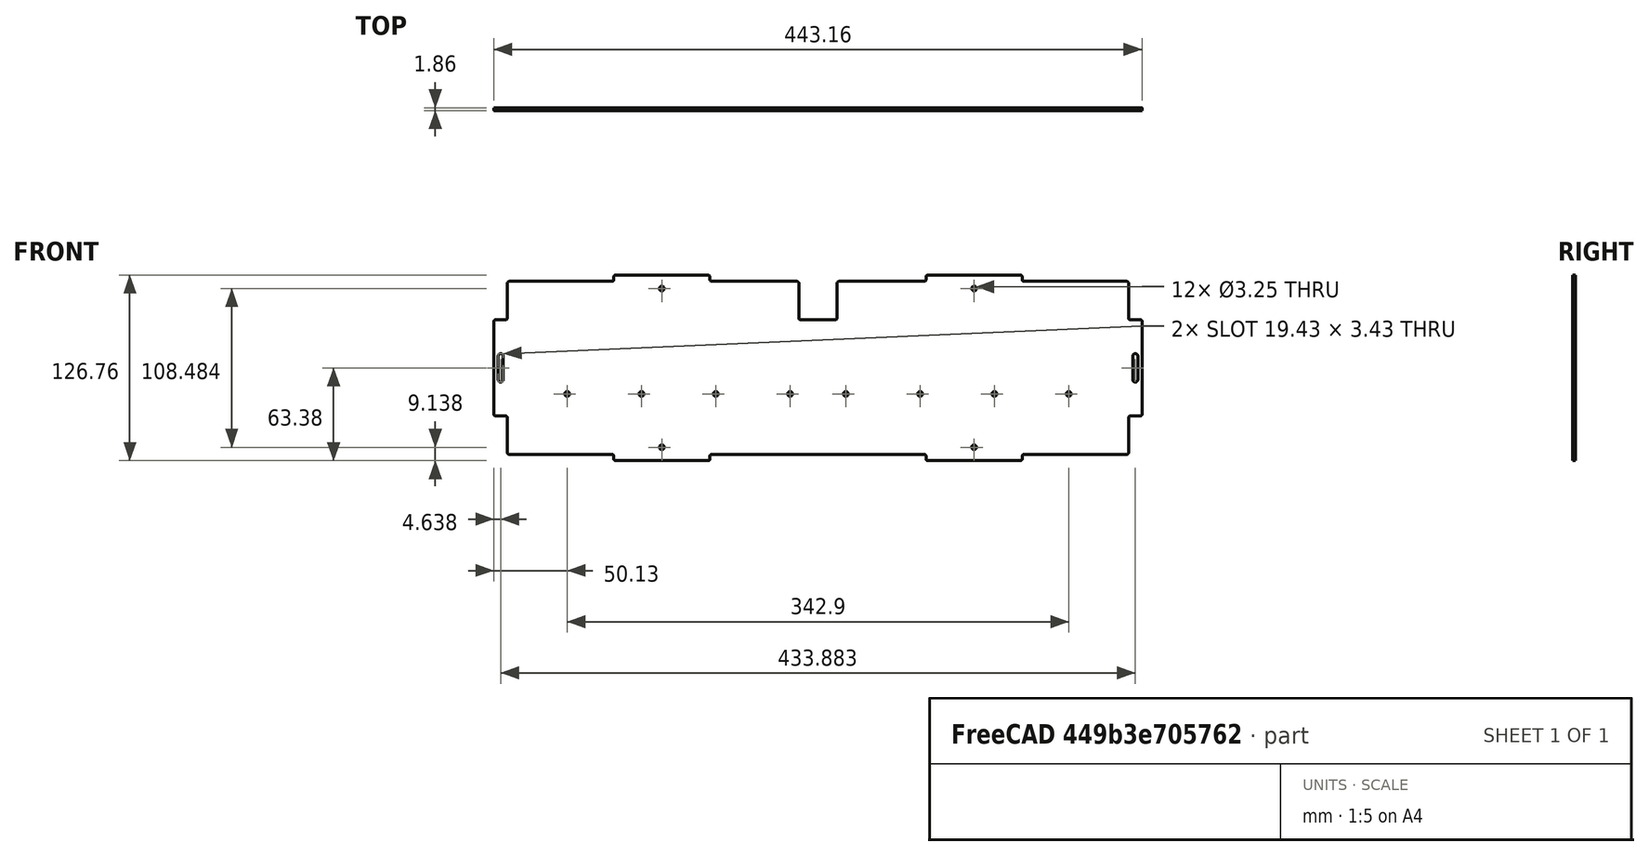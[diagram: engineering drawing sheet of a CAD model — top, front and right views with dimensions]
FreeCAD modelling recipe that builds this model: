
FCSTD DOCUMENT  (FreeCAD 1.0R38641 +468 (Git))
Label: panel_back
License: All rights reserved
LicenseURL: https://en.wikipedia.org/wiki/All_rights_reserved
objects: PartDesign::SubShapeBinder×4, Sketcher::SketchObject×1, PartDesign::Pad×1, PartDesign::Body×1
note: 10 computed .brp shape members not serialized (recipe doc carries the construction recipe); baked Part::Feature solids carry a one-line shape summary decoded from their .brp
EXTERNAL_REF file=dimensions.FCStd obj=VarSet
EXTERNAL_REF file=../third_party/doepfer_bus_board_v6.FCStd obj=Sketch
EXTERNAL_REF file=panel_top_and_bottom.FCStd obj=Body
EXTERNAL_REF file=panel_side.FCStd obj=Body001
EXTERNAL_REF file=../third_party/doepfer_bus_board_v6.FCStd obj=Body
EXTERNAL_REF file=../third_party/doepfer_psu3.FCStd obj=Body

FEATURE [PartDesign::SubShapeBinder] Binder  label="BottomPanelBinder"
  BindCopyOnChange = 0
  BindMode = 0
  ClaimChildren = false
  Context = -> Body [Binder.]
  Fuse = false
  MakeFace = true
  OffsetFill = false
  OffsetIntersection = false
  OffsetJoinType = 0
  OffsetOpenResult = false
  PartialLoad = false
  Refine = true
  Relative = true
  Support = -> [<external panel_top_and_bottom.FCStd>#Body[Pad.]]
  _Version = 2
FEATURE [PartDesign::SubShapeBinder] Binder001  label="SidePanelBinder"
  BindCopyOnChange = 0
  BindMode = 0
  ClaimChildren = false
  Context = -> Body [Binder001.]
  Fuse = false
  MakeFace = true
  OffsetFill = false
  OffsetIntersection = false
  OffsetJoinType = 0
  OffsetOpenResult = false
  PartialLoad = false
  Refine = true
  Relative = true
  Support = -> [<external panel_side.FCStd>#Body001]
  _Version = 2
FEATURE [PartDesign::SubShapeBinder] Binder002  label="BusBoardBinder"
  BindCopyOnChange = 0
  BindMode = 0
  ClaimChildren = false
  Context = -> Body [Binder002.]
  Fuse = false
  MakeFace = true
  OffsetFill = false
  OffsetIntersection = false
  OffsetJoinType = 0
  OffsetOpenResult = false
  PartialLoad = false
  Placement = pos=(0,0,0) rot=(1,0,0;1.5708rad)
  Refine = true
  Relative = true
  Support = -> [<external ../third_party/doepfer_bus_board_v6.FCStd>#Body]
  _Version = 2
FEATURE [PartDesign::SubShapeBinder] Binder003  label="PsuBinder"
  BindCopyOnChange = 0
  BindMode = 0
  ClaimChildren = false
  Context = -> Body [Binder003.]
  Fuse = false
  MakeFace = true
  OffsetFill = false
  OffsetIntersection = false
  OffsetJoinType = 0
  OffsetOpenResult = false
  PartialLoad = false
  Placement = pos=(0,0,0) rot=(1,0,0;1.5708rad)
  Refine = true
  Relative = false
  Support = -> [<external ../third_party/doepfer_psu3.FCStd>#Body]
  _Version = 2
FEATURE [Sketcher::SketchObject] Sketch
  ArcFitTolerance = 1e-06
  AttachmentOffset = pos=(0,0,0.127) rot=(0,0,1;0rad)
  AttachmentSupport = -> [Binder001,Binder]
  ExternalGeometry = -> [Binder001,Binder,Binder002,Binder003]
  FullyConstrained = true
  MakeInternals = false
  MapMode = 5
  Placement = pos=(0,127.227,2.68e-14) rot=(1,0,0;1.5708rad)
  expr: .AttachmentOffset.Base.z = dimensions#VarSet.EnclosureFinishThickness
  expr: Constraints[189] = dimensions#VarSet.EnclosureFinishThickness
  expr: Constraints[288] = doepfer_bus_board_v6#Sketch.Constraints.HoleDiameter + 2 * dimensions#VarSet.EnclosureFinishThickness
  expr: Constraints[41] = 2 * <<dimensions>>#VarSet.EnclosureFinishThickness
  expr: Constraints[47] = dimensions#VarSet.EnclosureCornerRadius
  expr: Constraints[82] = <<dimensions>>#VarSet.FrameTotalThickness - 2 * <<dimensions>>#VarSet.EnclosureFinishThickness
  expr: Constraints[83] = dimensions#VarSet.FrameMinWidth + dimensions#VarSet.FrameHoleDiameter + 2 * dimensions#VarSet.FrameFinishThickness
  expr: Constraints[84] = dimensions#VarSet.FrameTotalThickness + 2 * dimensions#VarSet.EnclosureFinishThickness
  sketch-geometry (148):
    g0: LineSegment [constr] StartX=1e-15 StartY=-23.125 StartZ=0 EndX=1e-15 EndY=-23.379 EndZ=0
    g1: LineSegment [constr] StartX=9e-16 StartY=-89.121 StartZ=0 EndX=9e-16 EndY=-89.375 EndZ=0
    g2: LineSegment StartX=1e-15 StartY=-23.379 StartZ=0 EndX=-6.8772 EndY=-23.379 EndZ=0
    g3: LineSegment StartX=-8.0772 StartY=-24.579 StartZ=0 EndX=-8.0772 EndY=-87.921 EndZ=0
    g4: LineSegment StartX=-6.8772 StartY=-89.121 StartZ=0 EndX=9e-16 EndY=-89.121 EndZ=0
    g5: LineSegment StartX=1.2 StartY=-90.321 StartZ=0 EndX=1.2 EndY=-114.173 EndZ=0
    g6: LineSegment StartX=425.8 StartY=-114.173 StartZ=0 EndX=425.8 EndY=-90.321 EndZ=0
    g7: LineSegment StartX=427 StartY=-89.121 StartZ=0 EndX=433.877 EndY=-89.121 EndZ=0
    g8: LineSegment StartX=435.077 StartY=-87.921 StartZ=0 EndX=435.077 EndY=-24.579 EndZ=0
    g9: LineSegment StartX=433.877 StartY=-23.379 StartZ=0 EndX=427 EndY=-23.379 EndZ=0
    g10: LineSegment StartX=425.8 StartY=-22.179 StartZ=0 EndX=425.8 EndY=1.6729 EndZ=0
    g11: LineSegment StartX=1.2 StartY=1.6729 StartZ=0 EndX=1.2 EndY=-22.179 EndZ=0
    g12: ArcOfCircle CenterX=424.6 CenterY=1.6729 CenterZ=0 NormalX=0 NormalY=0 NormalZ=1 AngleXU=0 Radius=1.2 StartAngle=0 EndAngle=1.5708
    g13: ArcOfCircle CenterX=427 CenterY=-22.179 CenterZ=0 NormalX=0 NormalY=0 NormalZ=1 AngleXU=0 Radius=1.2 StartAngle=3.14159 EndAngle=4.71239
    g14: ArcOfCircle CenterX=433.877 CenterY=-24.579 CenterZ=0 NormalX=0 NormalY=0 NormalZ=1 AngleXU=0 Radius=1.2 StartAngle=8e-16 EndAngle=1.5708
    g15: ArcOfCircle CenterX=433.877 CenterY=-87.921 CenterZ=0 NormalX=0 NormalY=0 NormalZ=1 AngleXU=0 Radius=1.2 StartAngle=4.71239 EndAngle=6.28319
    g16: ArcOfCircle CenterX=427 CenterY=-90.321 CenterZ=0 NormalX=0 NormalY=0 NormalZ=1 AngleXU=0 Radius=1.2 StartAngle=1.5708 EndAngle=3.14159
    g17: ArcOfCircle CenterX=424.6 CenterY=-114.173 CenterZ=0 NormalX=0 NormalY=0 NormalZ=1 AngleXU=0 Radius=1.2 StartAngle=4.71239 EndAngle=6.28319
    g18: ArcOfCircle CenterX=2.4 CenterY=-114.173 CenterZ=0 NormalX=0 NormalY=0 NormalZ=1 AngleXU=0 Radius=1.2 StartAngle=3.14159 EndAngle=4.71239
    g19: ArcOfCircle CenterX=9e-16 CenterY=-90.321 CenterZ=0 NormalX=0 NormalY=0 NormalZ=1 AngleXU=0 Radius=1.2 StartAngle=2.6e-15 EndAngle=1.5708
    g20: ArcOfCircle CenterX=-6.8772 CenterY=-87.921 CenterZ=0 NormalX=0 NormalY=0 NormalZ=1 AngleXU=0 Radius=1.2 StartAngle=3.14159 EndAngle=4.71239
    g21: ArcOfCircle CenterX=-6.8772 CenterY=-24.579 CenterZ=0 NormalX=0 NormalY=0 NormalZ=1 AngleXU=0 Radius=1.2 StartAngle=1.5708 EndAngle=3.14159
    g22: ArcOfCircle CenterX=1.2e-15 CenterY=-22.179 CenterZ=0 NormalX=0 NormalY=0 NormalZ=1 AngleXU=0 Radius=1.2 StartAngle=4.71239 EndAngle=6.28319
    g23: ArcOfCircle CenterX=2.4 CenterY=1.6729 CenterZ=0 NormalX=0 NormalY=0 NormalZ=1 AngleXU=0 Radius=1.2 StartAngle=1.5708 EndAngle=3.14159
    g24: ArcOfCircle CenterX=-3.4417 CenterY=-48.25 CenterZ=0 NormalX=0 NormalY=0 NormalZ=1 AngleXU=0 Radius=1.7145 StartAngle=8e-16 EndAngle=3.14159
    g25: ArcOfCircle CenterX=-3.4417 CenterY=-64.25 CenterZ=0 NormalX=0 NormalY=0 NormalZ=1 AngleXU=0 Radius=1.7145 StartAngle=3.14159 EndAngle=6.28319
    g26: LineSegment StartX=-1.7272 StartY=-48.25 StartZ=0 EndX=-1.7272 EndY=-64.25 EndZ=0
    g27: LineSegment StartX=-5.1562 StartY=-48.25 StartZ=0 EndX=-5.1562 EndY=-64.25 EndZ=0
    g28: LineSegment [constr] StartX=-3.4417 StartY=-48.25 StartZ=0 EndX=-3.4417 EndY=-23.379 EndZ=0
    g29: LineSegment [constr] StartX=-3.4417 StartY=-64.25 StartZ=0 EndX=-3.4417 EndY=-89.121 EndZ=0
    g30: LineSegment [constr] StartX=430.442 StartY=-23.379 StartZ=0 EndX=430.442 EndY=-48.25 EndZ=0
    g31: LineSegment [constr] StartX=430.442 StartY=-89.121 StartZ=0 EndX=430.442 EndY=-64.25 EndZ=0
    g32: ArcOfCircle CenterX=430.442 CenterY=-48.25 CenterZ=0 NormalX=0 NormalY=0 NormalZ=1 AngleXU=0 Radius=1.7145 StartAngle=-1.8e-15 EndAngle=3.14159
    g33: ArcOfCircle CenterX=430.442 CenterY=-64.25 CenterZ=0 NormalX=0 NormalY=0 NormalZ=1 AngleXU=0 Radius=1.7145 StartAngle=3.14159 EndAngle=6.28319
    g34: LineSegment StartX=432.156 StartY=-48.25 StartZ=0 EndX=432.156 EndY=-64.25 EndZ=0
    g35: LineSegment StartX=428.727 StartY=-48.25 StartZ=0 EndX=428.727 EndY=-64.25 EndZ=0
    g36: LineSegment [constr] StartX=-8.0772 StartY=-48.25 StartZ=0 EndX=-5.1562 EndY=-48.25 EndZ=0
    g37: LineSegment [constr] StartX=432.156 StartY=-48.25 StartZ=0 EndX=435.077 EndY=-48.25 EndZ=0
    g38: LineSegment StartX=72.679 StartY=2.8729 StartZ=0 EndX=2.4 EndY=2.8729 EndZ=0
    g39: LineSegment StartX=139.621 StartY=4.0729 StartZ=0 EndX=139.621 EndY=5.9271 EndZ=0
    g40: LineSegment StartX=138.421 StartY=7.1271 StartZ=0 EndX=75.079 EndY=7.1271 EndZ=0
    g41: LineSegment StartX=73.879 StartY=5.9271 StartZ=0 EndX=73.879 EndY=4.0729 EndZ=0
    g42: ArcOfCircle CenterX=72.679 CenterY=4.0729 CenterZ=0 NormalX=0 NormalY=0 NormalZ=1 AngleXU=0 Radius=1.2 StartAngle=4.71239 EndAngle=6.28319
    g43: ArcOfCircle CenterX=75.079 CenterY=5.9271 CenterZ=0 NormalX=0 NormalY=0 NormalZ=1 AngleXU=0 Radius=1.2 StartAngle=1.5708 EndAngle=3.14159
    g44: ArcOfCircle CenterX=138.421 CenterY=5.9271 CenterZ=0 NormalX=0 NormalY=0 NormalZ=1 AngleXU=0 Radius=1.2 StartAngle=1e-16 EndAngle=1.5708
    g45: ArcOfCircle CenterX=140.821 CenterY=4.0729 CenterZ=0 NormalX=0 NormalY=0 NormalZ=1 AngleXU=0 Radius=1.2 StartAngle=3.14159 EndAngle=4.71239
    g46: LineSegment StartX=353.121 StartY=4.0729 StartZ=0 EndX=353.121 EndY=5.9271 EndZ=0
    g47: LineSegment StartX=351.921 StartY=7.1271 StartZ=0 EndX=288.579 EndY=7.1271 EndZ=0
    g48: LineSegment StartX=287.379 StartY=5.9271 StartZ=0 EndX=287.379 EndY=4.0729 EndZ=0
    g49: ArcOfCircle CenterX=286.179 CenterY=4.0729 CenterZ=0 NormalX=0 NormalY=0 NormalZ=1 AngleXU=0 Radius=1.2 StartAngle=4.71239 EndAngle=6.28319
    g50: ArcOfCircle CenterX=288.579 CenterY=5.9271 CenterZ=0 NormalX=0 NormalY=0 NormalZ=1 AngleXU=0 Radius=1.2 StartAngle=1.5708 EndAngle=3.14159
    g51: ArcOfCircle CenterX=351.921 CenterY=5.9271 CenterZ=0 NormalX=0 NormalY=0 NormalZ=1 AngleXU=0 Radius=1.2 StartAngle=3e-16 EndAngle=1.5708
    g52: ArcOfCircle CenterX=354.321 CenterY=4.0729 CenterZ=0 NormalX=0 NormalY=0 NormalZ=1 AngleXU=0 Radius=1.2 StartAngle=3.14159 EndAngle=4.71239
    g53: LineSegment StartX=424.6 StartY=2.8729 StartZ=0 EndX=354.321 EndY=2.8729 EndZ=0
    g54: LineSegment StartX=2.4 StartY=-115.373 StartZ=0 EndX=72.679 EndY=-115.373 EndZ=0
    g55: LineSegment StartX=73.879 StartY=-116.573 StartZ=0 EndX=73.879 EndY=-118.427 EndZ=0
    g56: LineSegment StartX=75.079 StartY=-119.627 StartZ=0 EndX=138.421 EndY=-119.627 EndZ=0
    g57: LineSegment StartX=139.621 StartY=-118.427 StartZ=0 EndX=139.621 EndY=-116.573 EndZ=0
    g58: LineSegment StartX=140.821 StartY=-115.373 StartZ=0 EndX=286.179 EndY=-115.373 EndZ=0
    g59: LineSegment StartX=287.379 StartY=-116.573 StartZ=0 EndX=287.379 EndY=-118.427 EndZ=0
    g60: LineSegment StartX=288.579 StartY=-119.627 StartZ=0 EndX=351.921 EndY=-119.627 EndZ=0
    g61: ArcOfCircle CenterX=351.921 CenterY=-118.427 CenterZ=0 NormalX=0 NormalY=0 NormalZ=1 AngleXU=0 Radius=1.2 StartAngle=4.71239 EndAngle=6.28319
    g62: ArcOfCircle CenterX=288.579 CenterY=-118.427 CenterZ=0 NormalX=0 NormalY=0 NormalZ=1 AngleXU=0 Radius=1.2 StartAngle=3.14159 EndAngle=4.71239
    g63: ArcOfCircle CenterX=286.179 CenterY=-116.573 CenterZ=0 NormalX=0 NormalY=0 NormalZ=1 AngleXU=0 Radius=1.2 StartAngle=2.3e-15 EndAngle=1.5708
    g64: ArcOfCircle CenterX=140.821 CenterY=-116.573 CenterZ=0 NormalX=0 NormalY=0 NormalZ=1 AngleXU=0 Radius=1.2 StartAngle=1.5708 EndAngle=3.14159
    g65: ArcOfCircle CenterX=138.421 CenterY=-118.427 CenterZ=0 NormalX=0 NormalY=0 NormalZ=1 AngleXU=0 Radius=1.2 StartAngle=4.71239 EndAngle=6.28319
    g66: ArcOfCircle CenterX=75.079 CenterY=-118.427 CenterZ=0 NormalX=0 NormalY=0 NormalZ=1 AngleXU=0 Radius=1.2 StartAngle=3.14159 EndAngle=4.71239
    g67: ArcOfCircle CenterX=72.679 CenterY=-116.573 CenterZ=0 NormalX=0 NormalY=0 NormalZ=1 AngleXU=0 Radius=1.2 StartAngle=5.1e-15 EndAngle=1.5708
    g68: LineSegment StartX=353.121 StartY=-118.427 StartZ=0 EndX=353.121 EndY=-116.573 EndZ=0
    g69: ArcOfCircle CenterX=354.321 CenterY=-116.573 CenterZ=0 NormalX=0 NormalY=0 NormalZ=1 AngleXU=0 Radius=1.2 StartAngle=1.5708 EndAngle=3.14159
    g70: LineSegment StartX=354.321 StartY=-115.373 StartZ=0 EndX=424.6 EndY=-115.373 EndZ=0
    g71: LineSegment [constr] StartX=73.625 StartY=4.0729 StartZ=0 EndX=73.879 EndY=4.0729 EndZ=0
    g72: LineSegment [constr] StartX=139.621 StartY=4.0729 StartZ=0 EndX=139.875 EndY=4.0729 EndZ=0
    g73: LineSegment [constr] StartX=287.125 StartY=4.0729 StartZ=0 EndX=287.379 EndY=4.0729 EndZ=0
    g74: LineSegment [constr] StartX=353.121 StartY=4.0729 StartZ=0 EndX=353.375 EndY=4.0729 EndZ=0
    g75: Circle CenterX=194.45 CenterY=-74.03 CenterZ=0 NormalX=0 NormalY=0 NormalZ=1 AngleXU=0 Radius=1.627
    g76: Circle CenterX=232.55 CenterY=-74.03 CenterZ=0 NormalX=0 NormalY=0 NormalZ=1 AngleXU=0 Radius=1.627
    g77: Circle CenterX=283.35 CenterY=-74.03 CenterZ=0 NormalX=0 NormalY=0 NormalZ=1 AngleXU=0 Radius=1.627
    g78: Circle CenterX=334.15 CenterY=-74.03 CenterZ=0 NormalX=0 NormalY=0 NormalZ=1 AngleXU=0 Radius=1.627
    g79: Circle CenterX=384.95 CenterY=-74.03 CenterZ=0 NormalX=0 NormalY=0 NormalZ=1 AngleXU=0 Radius=1.627
    g80: Circle CenterX=143.65 CenterY=-74.03 CenterZ=0 NormalX=0 NormalY=0 NormalZ=1 AngleXU=0 Radius=1.627
    g81: Circle CenterX=92.85 CenterY=-74.03 CenterZ=0 NormalX=0 NormalY=0 NormalZ=1 AngleXU=0 Radius=1.627
    g82: Circle CenterX=42.05 CenterY=-74.03 CenterZ=0 NormalX=0 NormalY=0 NormalZ=1 AngleXU=0 Radius=1.627
    g83: LineSegment [constr] StartX=42.05 StartY=-74.03 StartZ=0 EndX=92.85 EndY=-74.03 EndZ=0
    g84: LineSegment [constr] StartX=92.85 StartY=-74.03 StartZ=0 EndX=143.65 EndY=-74.03 EndZ=0
    g85: LineSegment [constr] StartX=143.65 StartY=-74.03 StartZ=0 EndX=194.45 EndY=-74.03 EndZ=0
    g86: LineSegment [constr] StartX=194.45 StartY=-74.03 StartZ=0 EndX=232.55 EndY=-74.03 EndZ=0
    g87: LineSegment [constr] StartX=232.55 StartY=-74.03 StartZ=0 EndX=283.35 EndY=-74.03 EndZ=0
    g88: LineSegment [constr] StartX=283.35 StartY=-74.03 StartZ=0 EndX=334.15 EndY=-74.03 EndZ=0
    g89: LineSegment [constr] StartX=334.15 StartY=-74.03 StartZ=0 EndX=384.95 EndY=-74.03 EndZ=0
    g90: LineSegment [constr] StartX=176.53 StartY=3.175 StartZ=0 EndX=214.63 EndY=3.175 EndZ=0
    g91: LineSegment [constr] StartX=214.63 StartY=3.175 StartZ=0 EndX=265.43 EndY=3.175 EndZ=0
    g92: LineSegment [constr] StartX=367.03 StartY=3.175 StartZ=0 EndX=391.16 EndY=3.175 EndZ=0
    g93: LineSegment [constr] StartX=384.95 StartY=-74.03 StartZ=0 EndX=409.08 EndY=-74.03 EndZ=0
    g94: LineSegment [constr] StartX=384.95 StartY=-74.03 StartZ=0 EndX=384.95 EndY=-35.295 EndZ=0
    g95: LineSegment [constr] StartX=409.08 StartY=-35.295 StartZ=0 EndX=42.05 EndY=-35.295 EndZ=0
    g96: LineSegment [constr] StartX=42.05 StartY=-74.03 StartZ=0 EndX=42.05 EndY=-35.295 EndZ=0
    g97: LineSegment [constr] StartX=409.08 StartY=-74.03 StartZ=0 EndX=409.08 EndY=-35.295 EndZ=0
    g98: LineSegment [constr] StartX=367.03 StartY=3.175 StartZ=0 EndX=367.03 EndY=41.91 EndZ=0
    g99: LineSegment [constr] StartX=367.03 StartY=3.175 StartZ=0 EndX=367.03 EndY=-5.6e-14 EndZ=0
    g100: LineSegment [constr] StartX=384.95 StartY=-74.03 StartZ=0 EndX=384.95 EndY=-77.205 EndZ=0
    g101: LineSegment [constr] StartX=409.08 StartY=-74.03 StartZ=0 EndX=409.08 EndY=-77.205 EndZ=0
    g102: LineSegment [constr] StartX=384.95 StartY=-77.205 StartZ=0 EndX=409.08 EndY=-77.205 EndZ=0
    g103: LineSegment [constr] StartX=409.08 StartY=-35.295 StartZ=0 EndX=409.08 EndY=2.8729 EndZ=0
    g104: LineSegment [constr] StartX=409.08 StartY=-77.205 StartZ=0 EndX=409.08 EndY=-115.373 EndZ=0
    g105: LineSegment [constr] StartX=42.05 StartY=-74.03 StartZ=0 EndX=17.92 EndY=-74.03 EndZ=0
    g106: LineSegment [constr] StartX=17.92 StartY=-74.03 StartZ=0 EndX=17.92 EndY=-35.295 EndZ=0
    g107: LineSegment [constr] StartX=17.92 StartY=-35.295 StartZ=0 EndX=42.05 EndY=-35.295 EndZ=0
    g108: LineSegment [constr] StartX=17.92 StartY=-35.295 StartZ=0 EndX=-8.0772 EndY=-35.295 EndZ=0
    g109: LineSegment [constr] StartX=409.08 StartY=-35.295 StartZ=0 EndX=435.077 EndY=-35.295 EndZ=0
    g110: LineSegment [constr] StartX=314 StartY=-16.25 StartZ=0 EndX=314 EndY=-96.25 EndZ=0
    g111: LineSegment [constr] StartX=113 StartY=-16.25 StartZ=0 EndX=113 EndY=-96.25 EndZ=0
    g112: LineSegment [constr] StartX=113 StartY=-16.25 StartZ=0 EndX=314 EndY=-16.25 EndZ=0
    g113: LineSegment [constr] StartX=113 StartY=-96.25 StartZ=0 EndX=314 EndY=-96.25 EndZ=0
    g114: LineSegment [constr] StartX=106.75 StartY=-2.0081 StartZ=0 EndX=320.25 EndY=-2.0081 EndZ=0
    g115: LineSegment [constr] StartX=106.75 StartY=-110.492 StartZ=0 EndX=320.25 EndY=-110.492 EndZ=0
    g116: Circle CenterX=106.75 CenterY=-2.0081 CenterZ=0 NormalX=0 NormalY=0 NormalZ=1 AngleXU=0 Radius=1.627
    g117: Circle CenterX=106.75 CenterY=-110.492 CenterZ=0 NormalX=0 NormalY=0 NormalZ=1 AngleXU=0 Radius=1.627
    g118: Circle CenterX=320.25 CenterY=-110.492 CenterZ=0 NormalX=0 NormalY=0 NormalZ=1 AngleXU=0 Radius=1.627
    g119: Circle CenterX=320.25 CenterY=-2.0081 CenterZ=0 NormalX=0 NormalY=0 NormalZ=1 AngleXU=0 Radius=1.627
    g120: LineSegment [constr] StartX=286.179 StartY=2.8729 StartZ=0 EndX=354.321 EndY=2.8729 EndZ=0
    g121: LineSegment [constr] StartX=320.25 StartY=-3.6351 StartZ=0 EndX=320.25 EndY=-110.492 EndZ=0
    g122: LineSegment [constr] StartX=320.25 StartY=-0.3811 StartZ=0 EndX=320.25 EndY=2.8729 EndZ=0
    g123: LineSegment [constr] StartX=320.25 StartY=-0.3811 StartZ=0 EndX=320.25 EndY=-3.6351 EndZ=0
    g124: LineSegment [constr] StartX=72.679 StartY=2.8729 StartZ=0 EndX=140.821 EndY=2.8729 EndZ=0
    g125: LineSegment [constr] StartX=106.75 StartY=-2.0081 StartZ=0 EndX=106.75 EndY=-110.492 EndZ=0
    g126: LineSegment [constr] StartX=72.679 StartY=-115.373 StartZ=0 EndX=140.821 EndY=-115.373 EndZ=0
    g127: LineSegment [constr] StartX=286.179 StartY=-115.373 StartZ=0 EndX=354.321 EndY=-115.373 EndZ=0
    g128: LineSegment [constr] StartX=320.25 StartY=-115.373 StartZ=0 EndX=320.25 EndY=-110.492 EndZ=0
    g129: LineSegment [constr] StartX=106.75 StartY=-2.0081 StartZ=0 EndX=106.75 EndY=2.8729 EndZ=0
    g130: LineSegment [constr] StartX=106.75 StartY=-16.25 StartZ=0 EndX=113 EndY=-16.25 EndZ=0
    g131: LineSegment [constr] StartX=314 StartY=-16.25 StartZ=0 EndX=320.25 EndY=-16.25 EndZ=0
    g132: LineSegment [constr] StartX=113 StartY=-16.25 StartZ=0 EndX=113 EndY=-2.0081 EndZ=0
    g133: LineSegment [constr] StartX=113 StartY=-96.25 StartZ=0 EndX=113 EndY=-110.492 EndZ=0
    g134: LineSegment StartX=199.174 StartY=2.8729 StartZ=0 EndX=140.821 EndY=2.8729 EndZ=0
    g135: LineSegment StartX=200.374 StartY=-22.179 StartZ=0 EndX=200.374 EndY=1.6729 EndZ=0
    g136: LineSegment StartX=225.426 StartY=-23.379 StartZ=0 EndX=201.574 EndY=-23.379 EndZ=0
    g137: LineSegment StartX=286.179 StartY=2.8729 StartZ=0 EndX=227.826 EndY=2.8729 EndZ=0
    g138: LineSegment StartX=226.626 StartY=1.6729 StartZ=0 EndX=226.626 EndY=-22.179 EndZ=0
    g139: ArcOfCircle CenterX=199.174 CenterY=1.6729 CenterZ=0 NormalX=0 NormalY=0 NormalZ=1 AngleXU=0 Radius=1.2 StartAngle=1e-16 EndAngle=1.5708
    g140: GeomPoint [constr] X=200.374 Y=2.8729 Z=0
    g141: ArcOfCircle CenterX=201.574 CenterY=-22.179 CenterZ=0 NormalX=0 NormalY=0 NormalZ=1 AngleXU=0 Radius=1.2 StartAngle=3.14159 EndAngle=4.71239
    g142: GeomPoint [constr] X=200.374 Y=-23.379 Z=0
    g143: ArcOfCircle CenterX=225.426 CenterY=-22.179 CenterZ=0 NormalX=0 NormalY=0 NormalZ=1 AngleXU=0 Radius=1.2 StartAngle=4.71239 EndAngle=6.28319
    g144: GeomPoint [constr] X=226.626 Y=-23.379 Z=0
    g145: ArcOfCircle CenterX=227.826 CenterY=1.6729 CenterZ=0 NormalX=0 NormalY=0 NormalZ=1 AngleXU=0 Radius=1.2 StartAngle=1.5708 EndAngle=3.14159
    g146: GeomPoint [constr] X=226.626 Y=2.8729 Z=0
    g147: LineSegment [constr] StartX=213.5 StartY=-115.373 StartZ=0 EndX=213.5 EndY=-23.379 EndZ=0
  constraints (388):
    c: Equal(g1,g0)
    c: Horizontal(g2)
    c: Vertical(g3)
    c: Horizontal(g4)
    c: Vertical(g5)
    c: Vertical(g6)
    c: Horizontal(g7)
    c: Vertical(g8)
    c: Horizontal(g9)
    c: Vertical(g10)
    c: Vertical(g11)
    c: Tangent(g10,g12) = -1.5708
    c: Tangent(g9,g13) = 1.5708
    c: Tangent(g10,g13) = 1.5708
    c: Tangent(g8,g14) = -1.5708
    c: Tangent(g9,g14) = -1.5708
    c: Tangent(g7,g15) = -1.5708
    c: Tangent(g8,g15) = -1.5708
    c: Tangent(g6,g16) = 1.5708
    c: Tangent(g7,g16) = 1.5708
    c: Tangent(g6,g17) = -1.5708
    c: Tangent(g5,g18) = -1.5708
    c: Tangent(g4,g19) = 1.5708
    c: Tangent(g5,g19) = 1.5708
    c: Tangent(g3,g20) = -1.5708
    c: Tangent(g4,g20) = -1.5708
    c: Tangent(g2,g21) = -1.5708
    c: Tangent(g3,g21) = -1.5708
    c: Tangent(g2,g22) = 1.5708
    c: Tangent(g11,g22) = 1.5708
    c: Tangent(g11,g23) = -1.5708
    c: Equal(g12,g13)
    c: Equal(g13,g14)
    c: Equal(g14,g15)
    c: Equal(g15,g16)
    c: Equal(g16,g17)
    c: Equal(g18,g19)
    c: Equal(g19,g20)
    c: Equal(g20,g21)
    c: Equal(g21,g22)
    c: Equal(g22,g23)
    c: Distance(g1,g1) = 0.254
    c: Equal(g5,g11)
    c: Equal(g5,g6)
    c: Equal(g8,g3)
    c: Equal(g11,g10)
    c: Equal(g4,g7)
    c: Radius(g23) = 1.2
    c: Equal(g9,g7)
    c: Tangent(g24,g26) = 1.5708
    c: Tangent(g24,g27) = -1.5708
    c: Tangent(g25,g26) = 1.5708
    c: Tangent(g25,g27) = -1.5708
    c: Equal(g24,g25)
    c: Vertical(g26)
    c: Coincident(g29,g25)
    c: Vertical(g29)
    c: Equal(g28,g29)
    c: Coincident(g28,g24)
    c: Vertical(g28)
    c: PointOnObject(g30,g9)
    c: Vertical(g30)
    c: PointOnObject(g31,g7)
    c: Vertical(g31)
    c: Tangent(g32,g34) = 1.5708
    c: Tangent(g32,g35) = -1.5708
    c: Tangent(g33,g34) = 1.5708
    c: Tangent(g33,g35) = -1.5708
    c: Equal(g32,g33)
    c: Coincident(g32,g30)
    c: Coincident(g33,g31)
    c: Vertical(g34)
    c: Equal(g30,g31)
    c: Equal(g28,g30)
    c: Equal(g32,g24)
    c: PointOnObject(g36,g3)
    c: Coincident(g36,g24)
    c: Horizontal(g36)
    c: Coincident(g37,g32)
    c: PointOnObject(g37,g8)
    c: Horizontal(g37)
    c: Equal(g37,g36)
    c: Distance(g36,g36) = 2.921
    c: DistanceY(g27,g27) = 16
    c: Diameter(g24) = 3.429
    c: Vertical(g1)
    c: Vertical(g0)
    c: Horizontal(g53)
    c: Vertical(g46)
    c: Horizontal(g47)
    c: Vertical(g48)
    c: Vertical(g39)
    c: Horizontal(g40)
    c: Vertical(g41)
    c: Tangent(g41,g42) = 1.5708
    c: Tangent(g38,g42) = 1.5708
    c: Tangent(g40,g43) = -1.5708
    c: Tangent(g41,g43) = -1.5708
    c: Tangent(g39,g44) = -1.5708
    c: Tangent(g40,g44) = -1.5708
    c: Coincident(g134,g45) = 1.5708
    c: Tangent(g39,g45) = 1.5708
    c: Tangent(g48,g49) = 1.5708
    c: Tangent(g47,g50) = -1.5708
    c: Tangent(g48,g50) = -1.5708
    c: Tangent(g46,g51) = -1.5708
    c: Tangent(g47,g51) = -1.5708
    c: Tangent(g53,g52) = 1.5708
    c: Tangent(g46,g52) = 1.5708
    c: Equal(g42,g43)
    c: Equal(g43,g44)
    c: Equal(g44,g45)
    c: Equal(g45,g49)
    c: Equal(g49,g50)
    c: Equal(g51,g52)
    c: Equal(g50,g51)
    c: Equal(g48,g39)
    c: Horizontal(g38)
    c: Horizontal(g54)
    c: Vertical(g55)
    c: Horizontal(g56)
    c: Vertical(g57)
    c: Horizontal(g58)
    c: Vertical(g59)
    c: Horizontal(g60)
    c: Vertical(g68)
    c: Horizontal(g70)
    c: Tangent(g68,g69) = 1.5708
    c: Tangent(g70,g69) = 1.5708
    c: Tangent(g60,g61) = -1.5708
    c: Tangent(g68,g61) = -1.5708
    c: Tangent(g59,g62) = -1.5708
    c: Tangent(g60,g62) = -1.5708
    c: Tangent(g58,g63) = 1.5708
    c: Tangent(g59,g63) = 1.5708
    c: Tangent(g57,g64) = 1.5708
    c: Tangent(g58,g64) = 1.5708
    c: Tangent(g56,g65) = -1.5708
    c: Tangent(g57,g65) = -1.5708
    c: Tangent(g55,g66) = -1.5708
    c: Tangent(g56,g66) = -1.5708
    c: Tangent(g54,g67) = 1.5708
    c: Tangent(g55,g67) = 1.5708
    c: Equal(g69,g61)
    c: Equal(g61,g62)
    c: Equal(g62,g63)
    c: Equal(g64,g65)
    c: Equal(g65,g66)
    c: Equal(g66,g67)
    c: Equal(g57,g59)
    c: Equal(g54,g70)
    c: Tangent(g17,g70) = -1.5708
    c: Tangent(g12,g53) = -1.5708
    c: Tangent(g54,g18) = -1.5708
    c: Tangent(g23,g38) = -1.5708
    c: Coincident(g0,g2)
    c: Coincident(g1,g4)
    c: PointOnObject(g29,g4)
    c: PointOnObject(g28,g2)
    c: Coincident(g0,g-4)
    c: Coincident(g-4,g1)
    c: Equal(g23,g42)
    c: Equal(g18,g67)
    c: Equal(g63,g64)
    c: Coincident(g71,g41)
    c: Horizontal(g71)
    c: Equal(g71,g0)
    c: Coincident(g72,g39)
    c: Equal(g71,g72)
    c: Coincident(g73,g48)
    c: Coincident(g74,g46)
    c: Horizontal(g74)
    c: Equal(g74,g73)
    c: Equal(g73,g72)
    c: Distance(g73,g73) = 0.254
    c: Distance(g74,g74) = 0.254
    c: Distance(g72,g72) = 0.254
    c: Distance(g71,g71) = 0.254
    c: Distance(g0,g0) = 0.254
    c: Equal(g54,g38)
    c: Coincident(g74,g-6)
    c: Coincident(g73,g-6)
    c: Coincident(g72,g-5)
    c: Coincident(g71,g-5)
    c: Equal(g55,g41)
    c: Equal(g57,g55)
    c: Equal(g56,g40)
    c: Equal(g60,g47)
    c: Equal(g59,g68)
    c: Distance(g26,g-3) = 0.127
    c: PointOnObject(g41,g-8)
    c: DistanceX(g47,g47) = 63.342
    c: DistanceX(g40,g40) = 63.342
    c: DistanceY(g3,g3) = 63.342
    c: Equal(g82,g81)
    c: Equal(g81,g80)
    c: Equal(g80,g75)
    c: Equal(g75,g76)
    c: Equal(g76,g77)
    c: Equal(g77,g78)
    c: Equal(g78,g79)
    c: Coincident(g83,g82)
    c: Coincident(g83,g81)
    c: Horizontal(g83)
    c: Coincident(g84,g81)
    c: Coincident(g84,g80)
    c: Coincident(g85,g80)
    c: Coincident(g85,g75)
    c: Coincident(g86,g75)
    c: Coincident(g86,g76)
    c: Horizontal(g86)
    c: Coincident(g87,g76)
    c: Coincident(g87,g77)
    c: Coincident(g88,g77)
    c: Coincident(g88,g78)
    c: Horizontal(g88)
    c: Coincident(g89,g78)
    c: Coincident(g89,g79)
    c: Horizontal(g89)
    c: Horizontal(g87)
    c: Horizontal(g85)
    c: Horizontal(g84)
    c: Equal(g83,g84)
    c: Equal(g84,g85)
    c: Equal(g85,g87)
    c: Equal(g87,g88)
    c: Equal(g88,g89)
    c: Coincident(g90,g-9)
    c: Coincident(g90,g-10)
    c: Coincident(g91,g90)
    c: Coincident(g91,g-11)
    c: Equal(g90,g86)
    c: Equal(g91,g87)
    c: Coincident(g92,g-14)
    c: PointOnObject(g92,g-13)
    c: Horizontal(g92)
    c: Coincident(g93,g79)
    c: Horizontal(g93)
    c: Coincident(g94,g79)
    c: Vertical(g94)
    c: Horizontal(g95)
    c: Coincident(g96,g82)
    c: Coincident(g96,g95)
    c: Vertical(g96)
    c: Coincident(g97,g93)
    c: Coincident(g97,g95)
    c: Vertical(g97)
    c: PointOnObject(g94,g95)
    c: Coincident(g98,g92)
    c: PointOnObject(g98,g-12)
    c: Vertical(g98)
    c: Equal(g98,g94)
    c: Equal(g93,g92)
    c: Coincident(g99,g92)
    c: PointOnObject(g99,g-15)
    c: Vertical(g99)
    c: Coincident(g100,g79)
    c: Coincident(g101,g93)
    c: Vertical(g101)
    c: Coincident(g102,g100)
    c: Coincident(g102,g101)
    c: Vertical(g100)
    c: Horizontal(g102)
    c: Equal(g100,g99)
    c: Coincident(g103,g95)
    c: PointOnObject(g103,g53)
    c: Vertical(g103)
    c: Coincident(g104,g101)
    c: PointOnObject(g104,g70)
    c: Vertical(g104)
    c: Equal(g104,g103)
    c: Coincident(g105,g82)
    c: Horizontal(g105)
    c: Coincident(g106,g105)
    c: Vertical(g106)
    c: Coincident(g107,g95)
    c: Horizontal(g107)
    c: Coincident(g107,g106)
    c: Coincident(g108,g106)
    c: PointOnObject(g108,g3)
    c: Horizontal(g108)
    c: Coincident(g109,g95)
    c: PointOnObject(g109,g8)
    c: Horizontal(g109)
    c: Equal(g109,g108)
    c: Equal(g105,g93)
    c: DistanceX(g85,g85) = 50.8
    c: DistanceX(g86,g86) = 38.1
    c: Diameter(g80) = 3.254
    c: Vertical(g110)
    c: Vertical(g111)
    c: Coincident(g112,g111)
    c: Coincident(g112,g110)
    c: Coincident(g113,g111)
    c: Coincident(g113,g110)
    c: Horizontal(g113)
    c: Equal(g112,g-17)
    c: Equal(g110,g-16)
    c: Horizontal(g114)
    c: Horizontal(g115)
    c: Coincident(g117,g115)
    c: Coincident(g118,g115)
    c: Equal(g119,g118)
    c: Equal(g118,g117)
    c: Equal(g116,g117)
    c: Equal(g116,g80)
    c: Coincident(g120,g137)
    c: Coincident(g120,g52)
    c: Coincident(g121,g115)
    c: Vertical(g121)
    c: PointOnObject(g122,g119)
    c: PointOnObject(g122,g120)
    c: PointOnObject(g121,g119)
    c: Tangent(g121,g122)
    c: Coincident(g123,g122)
    c: Coincident(g123,g121)
    c: PointOnObject(g119,g123)
    c: Equal(g123,g122)
    c: Coincident(g114,g119)
    c: Equal(g114,g115)
    c: Coincident(g124,g38)
    c: Tangent(g124,g45) = -1.5708
    c: Coincident(g125,g115)
    c: Coincident(g126,g54)
    c: Coincident(g126,g58)
    c: Vertical(g128)
    c: Coincident(g128,g115)
    c: Symmetric(g127,g127,g128)
    c: Coincident(g127,g58)
    c: Coincident(g127,g69)
    c: Coincident(g125,g116)
    c: Coincident(g114,g116)
    c: Coincident(g129,g114)
    c: Symmetric(g124,g124,g129)
    c: Vertical(g129)
    c: Equal(g129,g128)
    c: PointOnObject(g130,g125)
    c: Coincident(g130,g111)
    c: Horizontal(g130)
    c: Coincident(g131,g110)
    c: PointOnObject(g131,g121)
    c: Horizontal(g131)
    c: Equal(g131,g130)
    c: Coincident(g132,g111)
    c: PointOnObject(g132,g114)
    c: Vertical(g132)
    c: Coincident(g133,g111)
    c: PointOnObject(g133,g115)
    c: Vertical(g133)
    c: Equal(g133,g132)
    c: Horizontal(g112)
    c: Horizontal(g134)
    c: Horizontal(g137)
    c: Vertical(g135)
    c: Vertical(g138)
    c: PointOnObject(g140,g134)
    c: PointOnObject(g140,g135)
    c: Tangent(g134,g139) = -1.5708
    c: Tangent(g135,g139) = -1.5708
    c: PointOnObject(g142,g135)
    c: PointOnObject(g142,g136)
    c: Tangent(g135,g141) = 1.5708
    c: Tangent(g136,g141) = 1.5708
    c: PointOnObject(g144,g136)
    c: PointOnObject(g144,g138)
    c: Tangent(g136,g143) = 1.5708
    c: Tangent(g138,g143) = 1.5708
    c: PointOnObject(g146,g137)
    c: PointOnObject(g146,g138)
    c: Tangent(g137,g145) = -1.5708
    c: Tangent(g138,g145) = -1.5708
    c: Equal(g145,g143)
    c: Equal(g143,g141)
    c: Equal(g139,g141)
    c: Equal(g139,g45)
    c: Symmetric(g58,g58,g147)
    c: Symmetric(g136,g136,g147)
    c: Vertical(g147)
    c: PointOnObject(g39,g-5)
    c: PointOnObject(g48,g-6)
    c: Tangent(g49,g120) = -1.5708
    c: Equal(g134,g137)
    c: Equal(g136,g138)
    c: Tangent(g136,g9)
    c: Distance(g8,g-2) = 435.077  'DeltaX'
    c: Distance(g60,g-1) = 119.627  'DeltaY'
    c: Distance(g3,g-2) = 8.0772  'OffsetX'
    c: Distance(g47,g-1) = 7.1271  'OffsetY'
FEATURE [PartDesign::Pad] Pad
  Direction = (0,-1,2e-16)
  Length = 1.8542
  Length2 = 10
  Placement = pos=(0,127.227,2.73e-14) rot=(1,0,0;1.5708rad)
  Profile = -> Sketch
  ReferenceAxis = -> Sketch [N_Axis]
  Refine = true
  Suppressed = false
  Type = 0
  expr: Length = <<dimensions>>#VarSet.EnclosureTotalThickness
FEATURE [PartDesign::Body] Body  label="PanelBack"
  AllowCompound = false
  Group = -> [Sketch,Pad,Binder001,Binder,Binder002,Binder003]
  Origin = -> Origin
  Tip = -> Pad
